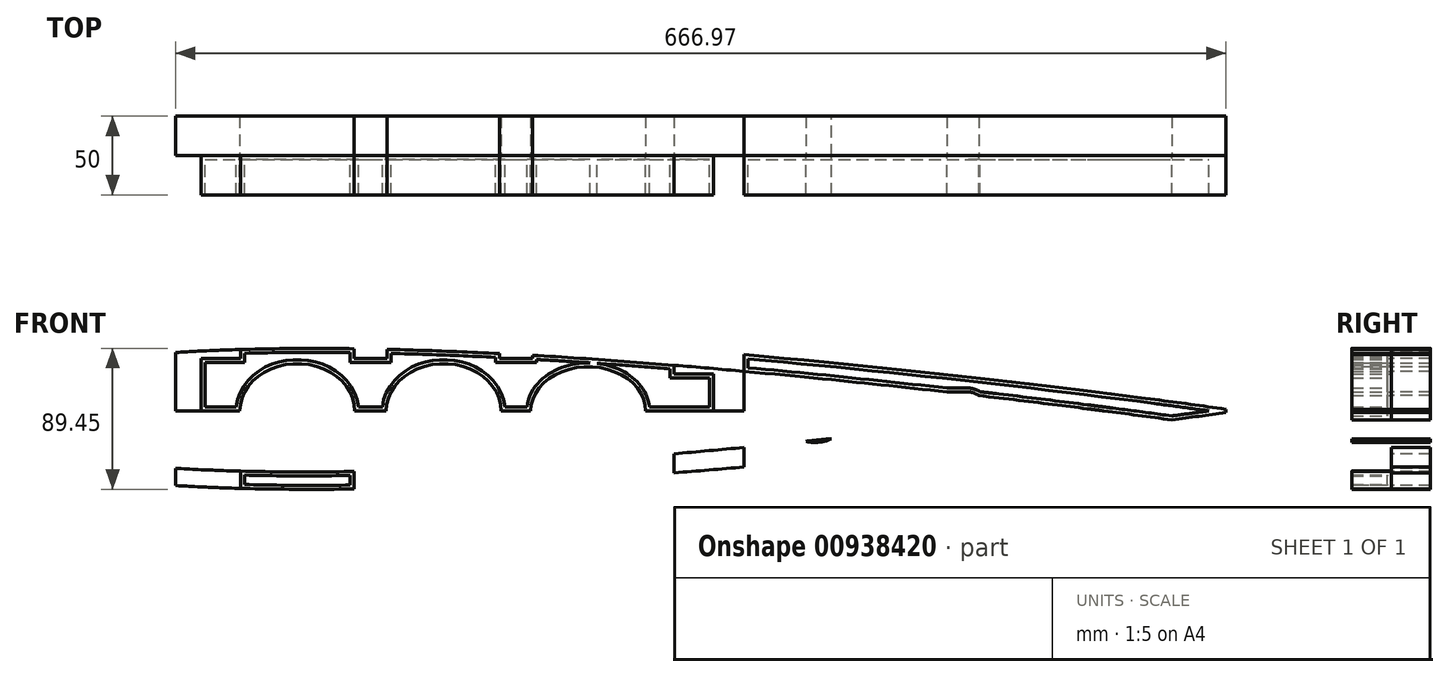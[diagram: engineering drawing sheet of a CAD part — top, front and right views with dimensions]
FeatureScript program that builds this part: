
annotation { "Feature Type Name" : "Feature", "Feature Type Description" : "" }
export const myFeature = defineFeature(function(context is Context, id is Id, definition is map)
    precondition{}
    {
        {
            var Q0;
            Q0=qCreatedBy(makeId("Front.planeOp"),FACE);
            var sketch = newSketch(context, id + "F0", { "sketchPlane" : qUnion([Q0])});
            skLineSegment(sketch, "E0", {"start": v(0, 0) * mm, "end": v(830, 0) * mm});
            skLineSegment(sketch, "E1", {"start": v(23.53, 0) * mm, "end": v(23.53, 22.98) * mm, "construction": true});
            skLineSegment(sketch, "E2", {"start": v(30.64, 0) * mm, "end": v(30.64, 25.86) * mm, "construction": true});
            skLineSegment(sketch, "E3", {"start": v(38.65, 0) * mm, "end": v(38.65, 28.62) * mm, "construction": true});
            skLineSegment(sketch, "E4", {"start": v(47.54, 0) * mm, "end": v(47.54, 31.24) * mm, "construction": true});
            skLineSegment(sketch, "E5", {"start": v(57.28, 0) * mm, "end": v(57.28, 33.72) * mm, "construction": true});
            skLineSegment(sketch, "E6", {"start": v(67.86, 0) * mm, "end": v(67.86, 36.05) * mm, "construction": true});
            skLineSegment(sketch, "E7", {"start": v(79.26, 0) * mm, "end": v(79.26, 38.22) * mm, "construction": true});
            skLineSegment(sketch, "E8", {"start": v(91.44, 0) * mm, "end": v(91.44, 40.22) * mm, "construction": true});
            skLineSegment(sketch, "E9", {"start": v(104.37, 0) * mm, "end": v(104.37, 42.04) * mm, "construction": true});
            skLineSegment(sketch, "E10", {"start": v(118.03, 0) * mm, "end": v(118.03, 43.68) * mm, "construction": true});
            skLineSegment(sketch, "E11", {"start": v(132.38, 0) * mm, "end": v(132.38, 45.13) * mm, "construction": true});
            skLineSegment(sketch, "E12", {"start": v(147.4, 0) * mm, "end": v(147.4, 46.38) * mm, "construction": true});
            skLineSegment(sketch, "E13", {"start": v(163.03, 0) * mm, "end": v(163.03, 47.45) * mm, "construction": true});
            skLineSegment(sketch, "E14", {"start": v(179.25, 0) * mm, "end": v(179.25, 48.31) * mm, "construction": true});
            skLineSegment(sketch, "E15", {"start": v(196.03, 0) * mm, "end": v(196.03, 48.98) * mm, "construction": true});
            skLineSegment(sketch, "E16", {"start": v(213.32, 0) * mm, "end": v(213.32, 49.45) * mm, "construction": true});
            skLineSegment(sketch, "E17", {"start": v(231.08, 0) * mm, "end": v(231.08, 49.73) * mm, "construction": true});
            skLineSegment(sketch, "E18", {"start": v(249.26, 0) * mm, "end": v(249.26, 49.81) * mm, "construction": true});
            skLineSegment(sketch, "E19", {"start": v(267.84, 0) * mm, "end": v(267.84, 49.72) * mm, "construction": true});
            skLineSegment(sketch, "E20", {"start": v(0.48, 0) * mm, "end": v(0.48, 3.54) * mm, "construction": true});
            skLineSegment(sketch, "E21", {"start": v(1.94, 0) * mm, "end": v(1.94, 7) * mm, "construction": true});
            skLineSegment(sketch, "E22", {"start": v(4.35, 0) * mm, "end": v(4.35, 10.38) * mm, "construction": true});
            skLineSegment(sketch, "E23", {"start": v(7.73, 0) * mm, "end": v(7.73, 13.67) * mm, "construction": true});
            skLineSegment(sketch, "E24", {"start": v(12.06, 0) * mm, "end": v(12.06, 16.87) * mm, "construction": true});
            skLineSegment(sketch, "E25", {"start": v(17.33, 0) * mm, "end": v(17.33, 19.98) * mm, "construction": true});
            skLineSegment(sketch, "E26", {"start": v(286.76, 0) * mm, "end": v(286.76, 49.45) * mm, "construction": true});
            skLineSegment(sketch, "E27", {"start": v(305.98, 0) * mm, "end": v(305.98, 49) * mm, "construction": true});
            skLineSegment(sketch, "E28", {"start": v(325.45, 0) * mm, "end": v(325.45, 48.4) * mm, "construction": true});
            skLineSegment(sketch, "E29", {"start": v(345.13, 0) * mm, "end": v(345.13, 47.64) * mm, "construction": true});
            skLineSegment(sketch, "E30", {"start": v(364.98, 0) * mm, "end": v(364.98, 46.75) * mm, "construction": true});
            skLineSegment(sketch, "E31", {"start": v(384.94, 0) * mm, "end": v(384.94, 45.71) * mm, "construction": true});
            skLineSegment(sketch, "E32", {"start": v(404.97, 0) * mm, "end": v(404.97, 44.56) * mm, "construction": true});
            skLineSegment(sketch, "E33", {"start": v(425.03, 0) * mm, "end": v(425.03, 43.3) * mm, "construction": true});
            skLineSegment(sketch, "E34", {"start": v(445.06, 0) * mm, "end": v(445.06, 41.93) * mm, "construction": true});
            skLineSegment(sketch, "E35", {"start": v(465.02, 0) * mm, "end": v(465.02, 40.47) * mm, "construction": true});
            skLineSegment(sketch, "E36", {"start": v(484.87, 0) * mm, "end": v(484.87, 38.94) * mm, "construction": true});
            skLineSegment(sketch, "E37", {"start": v(504.55, 0) * mm, "end": v(504.55, 37.33) * mm, "construction": true});
            skLineSegment(sketch, "E38", {"start": v(524.02, 0) * mm, "end": v(524.02, 35.67) * mm, "construction": true});
            skLineSegment(sketch, "E39", {"start": v(543.24, 0) * mm, "end": v(543.24, 33.96) * mm, "construction": true});
            skLineSegment(sketch, "E40", {"start": v(562.16, 0) * mm, "end": v(562.16, 32.21) * mm, "construction": true});
            skLineSegment(sketch, "E41", {"start": v(580.74, 0) * mm, "end": v(580.74, 30.44) * mm, "construction": true});
            skLineSegment(sketch, "E42", {"start": v(598.92, 0) * mm, "end": v(598.92, 28.64) * mm, "construction": true});
            skLineSegment(sketch, "E43", {"start": v(633.97, 0) * mm, "end": v(633.97, 25.03) * mm, "construction": true});
            skLineSegment(sketch, "E44", {"start": v(616.68, 0) * mm, "end": v(616.68, 26.83) * mm, "construction": true});
            skLineSegment(sketch, "E45", {"start": v(650.75, 0) * mm, "end": v(650.75, 23.23) * mm, "construction": true});
            skLineSegment(sketch, "E46", {"start": v(666.97, 0) * mm, "end": v(666.97, 21.44) * mm, "construction": true});
            skLineSegment(sketch, "E47", {"start": v(682.6, 0) * mm, "end": v(682.6, 19.68) * mm, "construction": true});
            skLineSegment(sketch, "E48", {"start": v(697.62, 0) * mm, "end": v(697.62, 17.96) * mm, "construction": true});
            skLineSegment(sketch, "E49", {"start": v(711.97, 0) * mm, "end": v(711.97, 16.27) * mm, "construction": true});
            skLineSegment(sketch, "E50", {"start": v(725.63, 0) * mm, "end": v(725.63, 14.64) * mm, "construction": true});
            skLineSegment(sketch, "E51", {"start": v(738.56, 0) * mm, "end": v(738.56, 13.06) * mm, "construction": true});
            skLineSegment(sketch, "E52", {"start": v(750.74, 0) * mm, "end": v(750.74, 11.55) * mm, "construction": true});
            skLineSegment(sketch, "E53", {"start": v(762.14, 0) * mm, "end": v(762.14, 10.11) * mm, "construction": true});
            skLineSegment(sketch, "E54", {"start": v(791.35, 0) * mm, "end": v(791.35, 6.32) * mm, "construction": true});
            skLineSegment(sketch, "E55", {"start": v(799.36, 0) * mm, "end": v(799.36, 5.25) * mm, "construction": true});
            skLineSegment(sketch, "E56", {"start": v(806.47, 0) * mm, "end": v(806.47, 4.29) * mm, "construction": true});
            skLineSegment(sketch, "E57", {"start": v(782.46, 0) * mm, "end": v(782.46, 7.49) * mm, "construction": true});
            skLineSegment(sketch, "E58", {"start": v(812.67, 0) * mm, "end": v(812.67, 3.45) * mm, "construction": true});
            skLineSegment(sketch, "E59", {"start": v(817.94, 0) * mm, "end": v(817.94, 2.72) * mm, "construction": true});
            skLineSegment(sketch, "E60", {"start": v(822.27, 0) * mm, "end": v(822.27, 2.12) * mm, "construction": true});
            skLineSegment(sketch, "E61", {"start": v(825.65, 0) * mm, "end": v(825.65, 1.65) * mm, "construction": true});
            skLineSegment(sketch, "E62", {"start": v(828.06, 0) * mm, "end": v(828.06, 1.32) * mm, "construction": true});
            skLineSegment(sketch, "E63", {"start": v(772.72, 0) * mm, "end": v(772.72, 8.76) * mm, "construction": true});
            skLineSegment(sketch, "E64", {"start": v(829.52, 0) * mm, "end": v(829.52, 1.11) * mm, "construction": true});
            skLineSegment(sketch, "E65", {"start": v(830, 0) * mm, "end": v(830, 1.05) * mm});
            skFitSpline(sketch, "E66", {"points": [v(0, 0) * mm, v(0.48, 3.54) * mm, v(1.94, 7) * mm, v(4.35, 10.38) * mm, v(7.73, 13.67) * mm, v(12.06, 16.87) * mm, v(17.33, 19.98) * mm, v(23.53, 22.98) * mm, v(30.64, 25.86) * mm, v(38.65, 28.62) * mm, v(47.54, 31.24) * mm, v(57.28, 33.72) * mm, v(67.86, 36.05) * mm, v(79.26, 38.22) * mm, v(91.44, 40.22) * mm, v(104.37, 42.04) * mm, v(118.03, 43.68) * mm, v(132.38, 45.13) * mm, v(147.4, 46.39) * mm, v(163.03, 47.45) * mm, v(179.25, 48.31) * mm, v(196.03, 48.98) * mm, v(213.32, 49.45) * mm, v(231.08, 49.73) * mm, v(249.26, 49.81) * mm, v(267.84, 49.72) * mm, v(286.76, 49.45) * mm, v(305.98, 49) * mm, v(325.45, 48.4) * mm, v(345.13, 47.64) * mm, v(364.98, 46.75) * mm, v(384.94, 45.71) * mm, v(404.97, 44.56) * mm, v(425.03, 43.3) * mm, v(445.06, 41.93) * mm, v(465.02, 40.47) * mm, v(484.87, 38.94) * mm, v(504.55, 37.33) * mm, v(524.02, 35.67) * mm, v(543.24, 33.96) * mm, v(562.16, 32.21) * mm, v(580.74, 30.44) * mm, v(598.92, 28.64) * mm, v(616.68, 26.83) * mm, v(633.97, 25.03) * mm, v(650.75, 23.23) * mm, v(666.97, 21.44) * mm, v(682.6, 19.68) * mm, v(697.62, 17.96) * mm, v(711.97, 16.27) * mm, v(725.63, 14.64) * mm, v(738.56, 13.06) * mm, v(750.74, 11.55) * mm, v(762.14, 10.11) * mm, v(772.72, 8.76) * mm, v(782.46, 7.49) * mm, v(791.35, 6.32) * mm, v(799.36, 5.25) * mm, v(806.47, 4.29) * mm, v(812.67, 3.45) * mm, v(817.94, 2.72) * mm, v(822.27, 2.12) * mm, v(825.65, 1.65) * mm, v(828.06, 1.32) * mm, v(829.52, 1.11) * mm, v(830, 1.05) * mm], "startDerivative": vector(34.1, 427.03) * mm, "endDerivative": vector(137.1, -19.25) * mm});
            skFitSpline(sketch, "E67.MirrorCS", {"points": [v(0, 0) * mm, v(0.48, -3.54) * mm, v(1.94, -7) * mm, v(4.35, -10.38) * mm, v(7.73, -13.67) * mm, v(12.06, -16.87) * mm, v(17.33, -19.98) * mm, v(23.53, -22.98) * mm, v(30.64, -25.86) * mm, v(38.65, -28.62) * mm, v(47.54, -31.24) * mm, v(57.28, -33.72) * mm, v(67.86, -36.05) * mm, v(79.26, -38.22) * mm, v(91.44, -40.22) * mm, v(104.37, -42.04) * mm, v(118.03, -43.68) * mm, v(132.38, -45.13) * mm, v(147.4, -46.39) * mm, v(163.03, -47.45) * mm, v(179.25, -48.31) * mm, v(196.03, -48.98) * mm, v(213.32, -49.45) * mm, v(231.08, -49.73) * mm, v(249.26, -49.81) * mm, v(267.84, -49.72) * mm, v(286.76, -49.45) * mm, v(305.98, -49) * mm, v(325.45, -48.4) * mm, v(345.13, -47.64) * mm, v(364.98, -46.75) * mm, v(384.94, -45.71) * mm, v(404.97, -44.56) * mm, v(425.03, -43.3) * mm, v(445.06, -41.93) * mm, v(465.02, -40.47) * mm, v(484.87, -38.94) * mm, v(504.55, -37.33) * mm, v(524.02, -35.67) * mm, v(543.24, -33.96) * mm, v(562.16, -32.21) * mm, v(580.74, -30.44) * mm, v(598.92, -28.64) * mm, v(616.68, -26.83) * mm, v(633.97, -25.03) * mm, v(650.75, -23.23) * mm, v(666.97, -21.44) * mm, v(682.6, -19.68) * mm, v(697.62, -17.96) * mm, v(711.97, -16.27) * mm, v(725.63, -14.64) * mm, v(738.56, -13.06) * mm, v(750.74, -11.55) * mm, v(762.14, -10.11) * mm, v(772.72, -8.76) * mm, v(782.46, -7.49) * mm, v(791.35, -6.32) * mm, v(799.36, -5.25) * mm, v(806.47, -4.29) * mm, v(812.67, -3.45) * mm, v(817.94, -2.72) * mm, v(822.27, -2.12) * mm, v(825.65, -1.65) * mm, v(828.06, -1.32) * mm, v(829.52, -1.11) * mm, v(830, -1.05) * mm], "startDerivative": vector(34.1, -427.03) * mm, "endDerivative": vector(137.1, 19.25) * mm});
            skLineSegment(sketch, "E68.MirrorCS", {"start": v(830, 0) * mm, "end": v(830, -1.05) * mm});
            skLineSegment(sketch, "E69", {"start": v(163.03, 47.45) * mm, "end": v(163.03, -47.45) * mm});
            skLineSegment(sketch, "E70", {"start": v(204.25, -49.23) * mm, "end": v(204.25, -33.23) * mm});
            skLineSegment(sketch, "E71", {"start": v(204.25, -33.23) * mm, "end": v(179.25, -33.23) * mm});
            skLineSegment(sketch, "E72", {"start": v(179.25, -33.23) * mm, "end": v(179.25, 33.23) * mm});
            skLineSegment(sketch, "E73", {"start": v(179.25, 33.23) * mm, "end": v(204.25, 33.23) * mm});
            skLineSegment(sketch, "E74", {"start": v(204.25, 33.23) * mm, "end": v(204.25, 49.23) * mm});
            skLineSegment(sketch, "E75", {"start": v(524.02, 35.67) * mm, "end": v(524.02, -35.67) * mm});
            skLineSegment(sketch, "E76", {"start": v(479.55, -39.36) * mm, "end": v(479.55, -23.36) * mm});
            skLineSegment(sketch, "E77", {"start": v(479.55, -23.36) * mm, "end": v(504.55, -23.36) * mm});
            skLineSegment(sketch, "E78", {"start": v(504.55, -23.36) * mm, "end": v(504.55, 23.36) * mm});
            skLineSegment(sketch, "E79", {"start": v(504.55, 23.36) * mm, "end": v(479.55, 23.36) * mm});
            skLineSegment(sketch, "E80", {"start": v(479.55, 23.36) * mm, "end": v(479.55, 39.36) * mm});
            skEllipse(sketch, "E81", {"center": v(240.25, 0) * mm, "majorRadius": 36.5 * mm, "minorRadius": 30 * mm, "majorAxis": v(1, 0)});
            skEllipse(sketch, "E82.1.0.0", {"center": v(333.25, 0) * mm, "majorRadius": 36.5 * mm, "minorRadius": 30 * mm, "majorAxis": v(1, 0)});
            skLineSegment(sketch, "E82.direction1", {"start": v(240.25, 0) * mm, "end": v(333.25, 0) * mm, "construction": true});
            skEllipse(sketch, "E83", {"center": v(425.03, 0) * mm, "majorRadius": 28 * mm, "minorRadius": 36.5 * mm, "majorAxis": v(0, -1)});
            skFitSpline(sketch, "E84.0", {"points": [v(19.9, 0) * mm, v(19.93, 0.28) * mm, v(19.97, 0.77) * mm, v(20.03, 1.33) * mm, v(20.07, 1.63) * mm, v(20.1, 1.78) * mm, v(20.12, 1.85) * mm, v(20.12, 1.88) * mm, v(20.13, 1.92) * mm, v(20.16, 1.99) * mm, v(20.2, 2.1) * mm, v(20.28, 2.3) * mm, v(20.43, 2.58) * mm, v(20.63, 2.94) * mm, v(20.87, 3.32) * mm, v(21.13, 3.7) * mm, v(21.53, 4.23) * mm, v(22.12, 4.91) * mm, v(22.98, 5.8) * mm, v(24.01, 6.71) * mm, v(25.19, 7.65) * mm, v(26.5, 8.6) * mm, v(28.4, 9.86) * mm, v(31.06, 11.42) * mm, v(34.64, 13.25) * mm, v(38.55, 15) * mm, v(44.15, 17.24) * mm, v(51.77, 19.86) * mm, v(61.74, 22.7) * mm, v(72.4, 25.26) * mm, v(83.62, 27.56) * mm, v(95.37, 29.62) * mm, v(107.56, 31.45) * mm, v(124.36, 33.6) * mm, v(146.26, 35.8) * mm, v(173.73, 37.69) * mm, v(202.17, 38.91) * mm, v(231.43, 39.53) * mm, v(261.35, 39.6) * mm, v(291.8, 39.18) * mm, v(322.69, 38.31) * mm, v(364.28, 36.62) * mm, v(416.8, 33.63) * mm, v(479.93, 28.95) * mm, v(531.98, 24.38) * mm, v(572.9, 20.44) * mm, v(603.14, 17.37) * mm, v(632.79, 14.2) * mm, v(661.73, 10.99) * mm, v(689.84, 7.73) * mm, v(716.93, 4.47) * mm, v(738.52, 1.78) * mm, v(755.07, -0.33) * mm, v(767.08, -1.9) * mm, v(778.65, -3.43) * mm, v(789.72, -4.91) * mm, v(800.24, -6.35) * mm, v(810.11, -7.7) * mm, v(817.7, -8.77) * mm, v(823.32, -9.57) * mm, v(826.6, -10.03) * mm, v(829.07, -10.39) * mm, v(830.84, -10.64) * mm, v(832.51, -10.88) * mm, v(834.08, -11.1) * mm, v(835.26, -11.27) * mm, v(836.14, -11.4) * mm, v(836.78, -11.5) * mm, v(837.37, -11.58) * mm, v(837.78, -11.64) * mm, v(838.05, -11.68) * mm, v(838.28, -11.71) * mm, v(838.4, -11.73) * mm, v(838.5, -11.74) * mm]});
            skFitSpline(sketch, "E85.MirrorCS", {"points": [v(19.9, 0) * mm, v(19.93, -0.28) * mm, v(19.97, -0.77) * mm, v(20.03, -1.33) * mm, v(20.08, -1.63) * mm, v(20.1, -1.78) * mm, v(20.12, -1.85) * mm, v(20.13, -1.87) * mm, v(20.14, -1.92) * mm, v(20.16, -1.99) * mm, v(20.2, -2.1) * mm, v(20.29, -2.29) * mm, v(20.44, -2.58) * mm, v(20.64, -2.94) * mm, v(20.88, -3.31) * mm, v(21.15, -3.7) * mm, v(21.55, -4.22) * mm, v(22.13, -4.9) * mm, v(23, -5.78) * mm, v(24.04, -6.7) * mm, v(25.22, -7.63) * mm, v(26.52, -8.57) * mm, v(28.44, -9.83) * mm, v(31.1, -11.38) * mm, v(34.7, -13.2) * mm, v(38.6, -14.93) * mm, v(44.21, -17.15) * mm, v(51.85, -19.74) * mm, v(61.83, -22.54) * mm, v(72.49, -25.06) * mm, v(83.73, -27.32) * mm, v(95.48, -29.34) * mm, v(107.68, -31.12) * mm, v(124.49, -33.22) * mm, v(146.4, -35.32) * mm, v(173.87, -37.11) * mm, v(202.32, -38.23) * mm, v(231.57, -38.74) * mm, v(261.5, -38.7) * mm, v(291.95, -38.16) * mm, v(322.83, -37.18) * mm, v(364.42, -35.33) * mm, v(416.93, -32.14) * mm, v(480.03, -27.22) * mm, v(532.07, -22.46) * mm, v(572.98, -18.36) * mm, v(603.2, -15.18) * mm, v(632.84, -11.91) * mm, v(661.77, -8.58) * mm, v(689.86, -5.22) * mm, v(716.95, -1.86) * mm, v(738.52, 0.91) * mm, v(755.06, 3.1) * mm, v(767.06, 4.7) * mm, v(778.63, 6.27) * mm, v(789.7, 7.8) * mm, v(800.21, 9.27) * mm, v(810.08, 10.67) * mm, v(817.67, 11.77) * mm, v(823.28, 12.58) * mm, v(826.56, 13.06) * mm, v(829.03, 13.42) * mm, v(830.8, 13.68) * mm, v(832.47, 13.93) * mm, v(834.03, 14.16) * mm, v(835.21, 14.33) * mm, v(836.1, 14.46) * mm, v(836.73, 14.56) * mm, v(837.32, 14.64) * mm, v(837.73, 14.7) * mm, v(838, 14.75) * mm, v(838.23, 14.78) * mm, v(838.36, 14.8) * mm, v(838.45, 14.81) * mm]});
            skLineSegment(sketch, "E86", {"start": v(100.03, 30.3) * mm, "end": v(134.03, 30.3) * mm});
            skLineSegment(sketch, "E87", {"start": v(140.03, 24.3) * mm, "end": v(140.03, -24.26) * mm});
            skLineSegment(sketch, "E88", {"start": v(133.98, -30.26) * mm, "end": v(100.03, -29.99) * mm});
            skPoint(sketch, "E89.visualSharp", {"position": v(140.03, 30.3) * mm});
            skArc(sketch, "E89.filletArc", {"start": v(140.03, 24.3) * mm, "mid": v(138.27, 28.55) * mm, "end": v(134.03, 30.3) * mm});
            skPoint(sketch, "E90.visualSharp", {"position": v(140.03, -30.3) * mm});
            skArc(sketch, "E90.filletArc", {"start": v(133.98, -30.26) * mm, "mid": v(138.25, -28.52) * mm, "end": v(140.03, -24.26) * mm});
            skEllipse(sketch, "E91", {"center": v(569.02, 0) * mm, "majorRadius": 20 * mm, "minorRadius": 22.5 * mm, "majorAxis": v(0, -1)});
            skLineSegment(sketch, "E92.bottom", {"start": v(625.97, -12) * mm, "end": v(665.97, -12) * mm});
            skLineSegment(sketch, "E92.top", {"start": v(625.97, 12) * mm, "end": v(665.97, 12) * mm});
            skLineSegment(sketch, "E92.left", {"start": v(623.97, -10) * mm, "end": v(623.97, 10) * mm});
            skLineSegment(sketch, "E92.right", {"start": v(665.97, -12) * mm, "end": v(665.97, 12) * mm});
            skPoint(sketch, "E92.middle", {"position": v(644.97, 0) * mm});
            skArc(sketch, "E93", {"start": v(665.97, 12) * mm, "mid": v(677.97, 0) * mm, "end": v(665.97, -12) * mm});
            skPoint(sketch, "E94.visualSharp", {"position": v(623.97, 12) * mm});
            skArc(sketch, "E94.filletArc", {"start": v(625.97, 12) * mm, "mid": v(624.56, 11.41) * mm, "end": v(623.97, 10) * mm});
            skPoint(sketch, "E95.visualSharp", {"position": v(623.97, -12) * mm});
            skArc(sketch, "E95.filletArc", {"start": v(623.97, -10) * mm, "mid": v(624.56, -11.41) * mm, "end": v(625.97, -12) * mm});
            skPoint(sketch, "E96", {"position": v(276.75, 0) * mm});
            skPoint(sketch, "E97", {"position": v(296.75, 0) * mm});
            skLineSegment(sketch, "E98.bottom", {"start": v(276.26, 65.67) * mm, "end": v(297.26, 65.67) * mm});
            skLineSegment(sketch, "E98.top", {"start": v(276.26, 33.23) * mm, "end": v(297.26, 33.23) * mm});
            skLineSegment(sketch, "E98.left", {"start": v(276.26, 65.67) * mm, "end": v(276.26, 33.23) * mm});
            skLineSegment(sketch, "E98.right", {"start": v(297.26, 65.67) * mm, "end": v(297.26, 33.23) * mm});
            skPoint(sketch, "E99", {"position": v(369.75, 0) * mm});
            skPoint(sketch, "E100", {"position": v(388.53, 0) * mm});
            skLineSegment(sketch, "E101", {"start": v(379.14, 0) * mm, "end": v(379.14, 46.03) * mm, "construction": true});
            skLineSegment(sketch, "E102.bottom", {"start": v(368.64, 58.81) * mm, "end": v(389.64, 58.81) * mm});
            skLineSegment(sketch, "E102.top", {"start": v(368.64, 33.23) * mm, "end": v(389.64, 33.23) * mm});
            skLineSegment(sketch, "E102.left", {"start": v(368.64, 58.81) * mm, "end": v(368.64, 33.23) * mm});
            skLineSegment(sketch, "E102.right", {"start": v(389.64, 58.81) * mm, "end": v(389.64, 33.23) * mm});
            skLineSegment(sketch, "E103.MirrorCS", {"start": v(297.26, -65.67) * mm, "end": v(297.26, -33.23) * mm});
            skLineSegment(sketch, "E104.MirrorCS", {"start": v(276.26, -65.67) * mm, "end": v(297.26, -65.67) * mm});
            skLineSegment(sketch, "E105.MirrorCS", {"start": v(276.26, -65.67) * mm, "end": v(276.26, -33.23) * mm});
            skLineSegment(sketch, "E106.MirrorCS", {"start": v(276.26, -33.23) * mm, "end": v(297.26, -33.23) * mm});
            skLineSegment(sketch, "E107.MirrorCS", {"start": v(368.64, -58.81) * mm, "end": v(389.64, -58.81) * mm});
            skLineSegment(sketch, "E108.MirrorCS", {"start": v(368.64, -58.81) * mm, "end": v(368.64, -33.23) * mm});
            skLineSegment(sketch, "E109.MirrorCS", {"start": v(389.64, -58.81) * mm, "end": v(389.64, -33.23) * mm});
            skLineSegment(sketch, "E110.MirrorCS", {"start": v(368.64, -33.23) * mm, "end": v(389.64, -33.23) * mm});
            skSolve(sketch);
        }
        {
            var Q0;
            {var subQ0=sQuery(id+"F0.wireOp",EDGE,"E73");Q0=makeQuery(id+"F0.imprint","IMPRINT",FACE,{"disambiguationData":[TD([[makeQuery(id+"F0.imprint","IMPRINT",EDGE,{"derivedFrom":subQ0}),-1.0]])]});}
            var Q1;
            {var subQ4=sQuery(id+"F0.wireOp",EDGE,"E70");Q1=makeQuery(id+"F0.imprint","IMPRINT",FACE,{"disambiguationData":[TD([[makeQuery(id+"F0.imprint","IMPRINT",EDGE,{"derivedFrom":subQ4}),-1.0]])]});}
            var Q2;
            {var subQ5=sQuery(id+"F0.wireOp",EDGE,"E84.0");Q2=makeQuery(id+"F0.imprint","IMPRINT",FACE,{"disambiguationData":[TD([[makeQuery(id+"F0.imprint","IMPRINT",EDGE,{"derivedFrom":subQ5}),1.0]])]});}
            var Q3;
            {var subQ6=sQuery(id+"F0.wireOp",EDGE,"E85.MirrorCS");Q3=makeQuery(id+"F0.imprint","IMPRINT",FACE,{"disambiguationData":[TD([[makeQuery(id+"F0.imprint","IMPRINT",EDGE,{"derivedFrom":subQ6}),-1.0]])]});}
            var Q4;
            {var subQ8=sQuery(id+"F0.wireOp",EDGE,"E68.MirrorCS");Q4=makeQuery(id+"F0.imprint","IMPRINT",FACE,{"disambiguationData":[TD([[makeQuery(id+"F0.imprint","IMPRINT",EDGE,{"derivedFrom":subQ8}),-1.0]])]});}
            var Q5;
            {var subQ11=sQuery(id+"F0.wireOp",EDGE,"E65");Q5=makeQuery(id+"F0.imprint","IMPRINT",FACE,{"disambiguationData":[TD([[makeQuery(id+"F0.imprint","IMPRINT",EDGE,{"derivedFrom":subQ11}),1.0]])]});}
            extrude(context, id + "F1", {"entities" : qUnion([Q0, Q1, Q2, Q3, Q4, Q5]), "depth" : 25 * mm, "offsetDistance" : 25 * mm});
        }
        {
            var Q0;
            {var subQ6=sQuery(id+"F0.wireOp",EDGE,"E85.MirrorCS");Q0=makeQuery(id+"F0.imprint","IMPRINT",FACE,{"disambiguationData":[TD([[makeQuery(id+"F0.imprint","IMPRINT",EDGE,{"derivedFrom":subQ6}),-1.0]])]});}
            var Q1;
            {var subQ5=sQuery(id+"F0.wireOp",EDGE,"E84.0");Q1=makeQuery(id+"F0.imprint","IMPRINT",FACE,{"disambiguationData":[TD([[makeQuery(id+"F0.imprint","IMPRINT",EDGE,{"derivedFrom":subQ5}),1.0]])]});}
            var Q2;
            {var subQ4=sQuery(id+"F0.wireOp",EDGE,"E73");Q2=makeQuery(id+"F0.imprint","IMPRINT",FACE,{"disambiguationData":[TD([[makeQuery(id+"F0.imprint","IMPRINT",EDGE,{"derivedFrom":subQ4}),1.0]])]});}
            var Q3;
            {var subQ0=sQuery(id+"F0.wireOp",EDGE,"E70");Q3=makeQuery(id+"F0.imprint","IMPRINT",FACE,{"disambiguationData":[TD([[makeQuery(id+"F0.imprint","IMPRINT",EDGE,{"derivedFrom":subQ0}),1.0]])]});}
            var Q4;
            {var subQ4=sQuery(id+"F0.wireOp",EDGE,"E70");Q4=makeQuery(id+"F0.imprint","IMPRINT",FACE,{"disambiguationData":[TD([[makeQuery(id+"F0.imprint","IMPRINT",EDGE,{"derivedFrom":subQ4}),-1.0]])]});}
            var Q5;
            {var subQ0=sQuery(id+"F0.wireOp",EDGE,"E73");Q5=makeQuery(id+"F0.imprint","IMPRINT",FACE,{"disambiguationData":[TD([[makeQuery(id+"F0.imprint","IMPRINT",EDGE,{"derivedFrom":subQ0}),-1.0]])]});}
            var Q6;
            {var subQ0=sQuery(id+"F0.wireOp",EDGE,"E79");Q6=makeQuery(id+"F0.imprint","IMPRINT",FACE,{"disambiguationData":[TD([[makeQuery(id+"F0.imprint","IMPRINT",EDGE,{"derivedFrom":subQ0}),-1.0]])]});}
            var Q7;
            {var subQ0=sQuery(id+"F0.wireOp",EDGE,"E76");Q7=makeQuery(id+"F0.imprint","IMPRINT",FACE,{"disambiguationData":[TD([[makeQuery(id+"F0.imprint","IMPRINT",EDGE,{"derivedFrom":subQ0}),-1.0]])]});}
            var Q8;
            {var subQ8=sQuery(id+"F0.wireOp",EDGE,"E68.MirrorCS");Q8=makeQuery(id+"F0.imprint","IMPRINT",FACE,{"disambiguationData":[TD([[makeQuery(id+"F0.imprint","IMPRINT",EDGE,{"derivedFrom":subQ8}),-1.0]])]});}
            var Q9;
            {var subQ11=sQuery(id+"F0.wireOp",EDGE,"E65");Q9=makeQuery(id+"F0.imprint","IMPRINT",FACE,{"disambiguationData":[TD([[makeQuery(id+"F0.imprint","IMPRINT",EDGE,{"derivedFrom":subQ11}),1.0]])]});}
            extrude(context, id + "F2", {"entities" : qUnion([Q0, Q1, Q2, Q3, Q4, Q5, Q6, Q7, Q8, Q9]), "oppositeDirection" : true, "depth" : 25 * mm, "offsetDistance" : 25 * mm});
        }
        {
            var Q0;
            Q0=makeQuery(id+"F1.opExtrude","CAP_FACE",FACE,{"disambiguationData":[OSD([sQuery(id+"F0.wireOp",EDGE,"E66"),sQuery(id+"F0.wireOp",EDGE,"E67.MirrorCS"),sQuery(id+"F0.wireOp",EDGE,"E69"),sQuery(id+"F0.wireOp",EDGE,"E84.0"),sQuery(id+"F0.wireOp",EDGE,"E85.MirrorCS"),sQuery(id+"F0.wireOp",EDGE,"E86"),sQuery(id+"F0.wireOp",EDGE,"E87"),sQuery(id+"F0.wireOp",EDGE,"E88"),sQuery(id+"F0.wireOp",EDGE,"E89.filletArc"),sQuery(id+"F0.wireOp",EDGE,"E90.filletArc")])],"isStart":false});
            var Q1;
            Q1=makeQuery(id+"F1.opExtrude","CAP_FACE",FACE,{"disambiguationData":[OSD([sQuery(id+"F0.wireOp",EDGE,"E66"),sQuery(id+"F0.wireOp",EDGE,"E67.MirrorCS"),sQuery(id+"F0.wireOp",EDGE,"E70"),sQuery(id+"F0.wireOp",EDGE,"E71"),sQuery(id+"F0.wireOp",EDGE,"E72"),sQuery(id+"F0.wireOp",EDGE,"E73"),sQuery(id+"F0.wireOp",EDGE,"E74"),sQuery(id+"F0.wireOp",EDGE,"E76"),sQuery(id+"F0.wireOp",EDGE,"E77"),sQuery(id+"F0.wireOp",EDGE,"E78"),sQuery(id+"F0.wireOp",EDGE,"E79"),sQuery(id+"F0.wireOp",EDGE,"E80"),sQuery(id+"F0.wireOp",EDGE,"E81"),sQuery(id+"F0.wireOp",EDGE,"E82.1.0.0"),sQuery(id+"F0.wireOp",EDGE,"E83"),sQuery(id+"F0.wireOp",EDGE,"E98.top"),sQuery(id+"F0.wireOp",EDGE,"E98.left"),sQuery(id+"F0.wireOp",EDGE,"E98.right"),sQuery(id+"F0.wireOp",EDGE,"E102.top"),sQuery(id+"F0.wireOp",EDGE,"E102.left"),sQuery(id+"F0.wireOp",EDGE,"E102.right"),sQuery(id+"F0.wireOp",EDGE,"E103.MirrorCS"),sQuery(id+"F0.wireOp",EDGE,"E105.MirrorCS"),sQuery(id+"F0.wireOp",EDGE,"E106.MirrorCS"),sQuery(id+"F0.wireOp",EDGE,"E108.MirrorCS"),sQuery(id+"F0.wireOp",EDGE,"E109.MirrorCS"),sQuery(id+"F0.wireOp",EDGE,"E110.MirrorCS")])],"isStart":false});
            var Q2;
            Q2=makeQuery(id+"F1.opExtrude","CAP_FACE",FACE,{"disambiguationData":[OSD([sQuery(id+"F0.wireOp",EDGE,"E65"),sQuery(id+"F0.wireOp",EDGE,"E66"),sQuery(id+"F0.wireOp",EDGE,"E67.MirrorCS"),sQuery(id+"F0.wireOp",EDGE,"E68.MirrorCS"),sQuery(id+"F0.wireOp",EDGE,"E75"),sQuery(id+"F0.wireOp",EDGE,"E91"),sQuery(id+"F0.wireOp",EDGE,"E92.bottom"),sQuery(id+"F0.wireOp",EDGE,"E92.top"),sQuery(id+"F0.wireOp",EDGE,"E92.left"),sQuery(id+"F0.wireOp",EDGE,"E93"),sQuery(id+"F0.wireOp",EDGE,"E94.filletArc"),sQuery(id+"F0.wireOp",EDGE,"E95.filletArc")])],"isStart":false});
            shell(context, id + "F3", {"entities" : qUnion([Q0, Q1, Q2]), "thickness" : 2.5 * mm});
        }
    });
